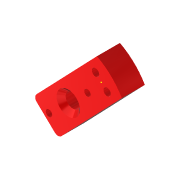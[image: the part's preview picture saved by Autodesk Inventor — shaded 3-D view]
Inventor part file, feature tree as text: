
AUTODESK INVENTOR PART (.ipt)
format: ipt  version: 2022 (Build 260153000, 153)  size: 118,272 bytes
history: native  units: mm
features: reference x5, other x5, sketch x3, extrude x1, fillet x1
ambient origin geometry x8: Origin, YZ Plane, XZ Plane, XY Plane, X Axis, Y Axis, Z Axis, Center Point
bodies: Volumenkörper1 (feature_tree)
feature tree (15):
  extrude  "Extrusion1"  Depth=6.2mm
  sketch  "Skizze2"  dims[d3=3.2mm]
  sketch  "Skizze3"  dims[d4=15.0mm d5=0.0mm d9=2.0mm]
  fillet  "Rundung1"  Radius=3.2mm
  sketch  "Skizze1"  dims[d0=30.0mm d1=6.2mm d2=3.2mm]
  reference  "Referenz1"
  reference  "Referenz2"
  reference  "Referenz3"
  reference  "Referenz4"
  reference  "Referenz5"
  other  "Assembly_Matchboxscope_injectionmolded_holo.iam"
  other  "IM_Matchboxscope_Laserholder:1"
  other  "00_laserpointer_red:2"
  other  "00_mk8_nozzle_0.4STEP:1"
  other  "IM_Lensholder:1"
